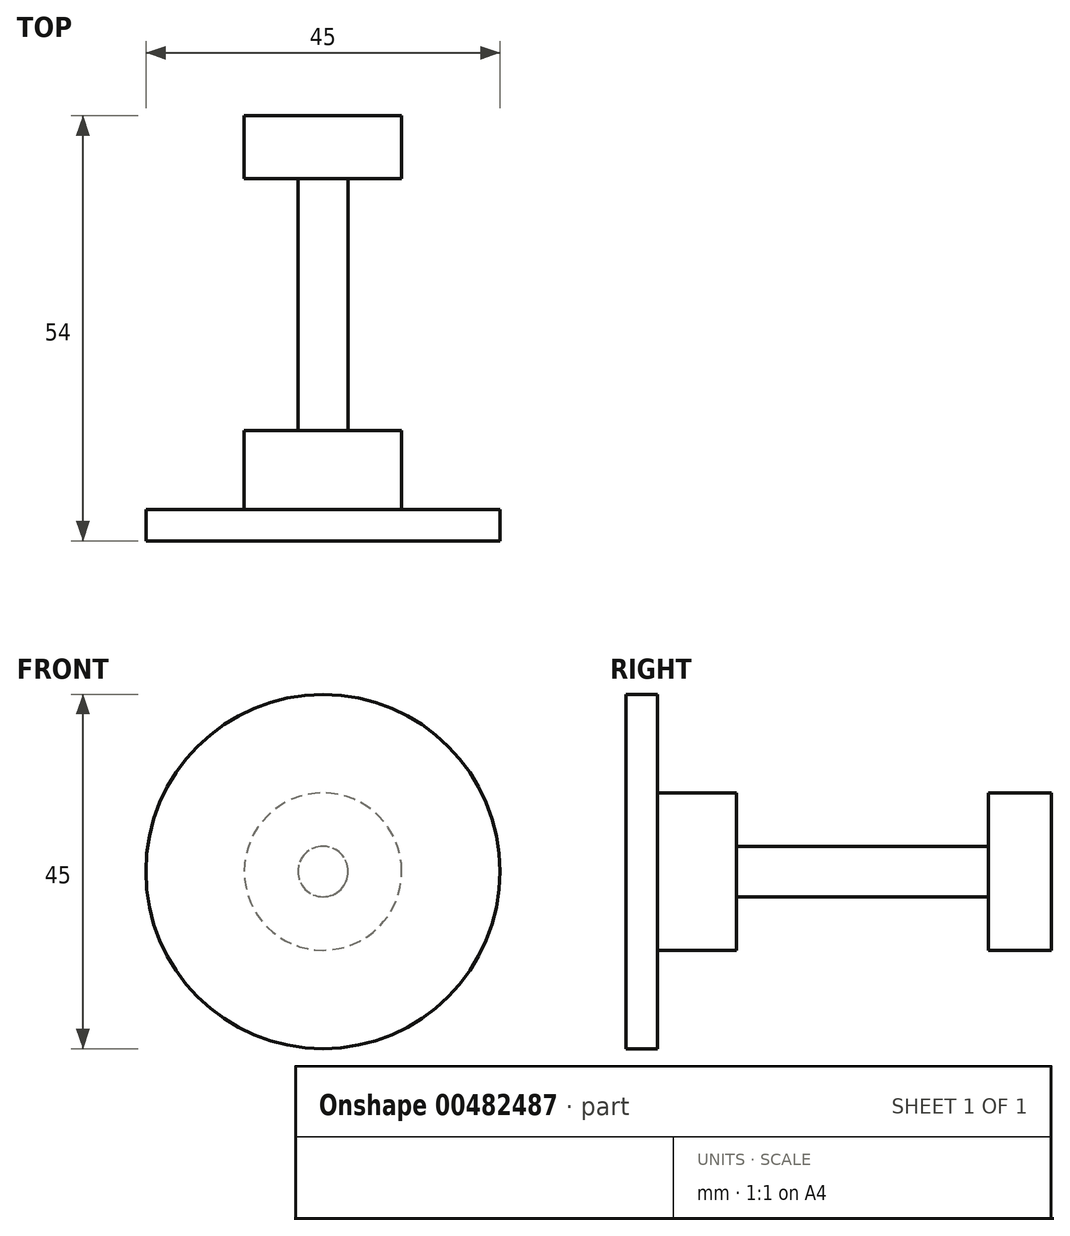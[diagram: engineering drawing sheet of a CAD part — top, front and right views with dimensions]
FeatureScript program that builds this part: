
annotation { "Feature Type Name" : "Feature", "Feature Type Description" : "" }
export const myFeature = defineFeature(function(context is Context, id is Id, definition is map)
    precondition{}
    {
        {
            var Q0;
            Q0=qCreatedBy(makeId("Front.planeOp"),FACE);
            var sketch = newSketch(context, id + "F0", { "sketchPlane" : qUnion([Q0])});
            skCircle(sketch, "E0", {"center": v(-28.73, 70.56) * mm, "radius": 3.2 * mm});
            skSolve(sketch);
        }
        {
            var Q0;
            Q0 = qSketchRegion(id + "F0", true);
            extrude(context, id + "F1", {"entities" : qUnion([Q0]), "depth" : 40 * mm, "offsetDistance" : 25 * mm, "symmetric" : true});
        }
        {
            var Q0;
            Q0=makeQuery(id+"F1.opExtrude","CAP_FACE",FACE,{"disambiguationData":[OSD([sQuery(id+"F0.wireOp",EDGE,"E0")])],"isStart":false});
            var sketch = newSketch(context, id + "F2", { "sketchPlane" : qUnion([Q0])});
            skCircle(sketch, "E1", {"center": v(-28.73, 70.56) * mm, "radius": 10 * mm});
            skSolve(sketch);
        }
        {
            var Q0;
            Q0 = qSketchRegion(id + "F2", true);
            extrude(context, id + "F3", {"entities" : qUnion([Q0]), "operationType" : NewBodyOperationType.ADD, "depth" : 10 * mm, "offsetDistance" : 25 * mm});
        }
        {
            var Q0;
            Q0=makeQuery(id+"F3.opExtrude","CAP_FACE",FACE,{"disambiguationData":[OSD([sQuery(id+"F2.wireOp",EDGE,"E1")])],"isStart":false});
            var sketch = newSketch(context, id + "F4", { "sketchPlane" : qUnion([Q0])});
            skCircle(sketch, "E2", {"center": v(-28.73, 70.56) * mm, "radius": 22.5 * mm});
            skSolve(sketch);
        }
        {
            var Q0;
            Q0=makeQuery(id+"F4.imprint","IMPRINT",FACE,{"disambiguationData":[TD([[makeQuery(id+"F4.imprint","IMPRINT",EDGE,{"derivedFrom":makeQuery(id+"F3.opExtrude","CAP_EDGE",EDGE,{"disambiguationData":[OSD([sQuery(id+"F2.wireOp",EDGE,"E1")])],"isStart":false})}),1.0]])]});
            var Q1;
            Q1=makeQuery(id+"F4.imprint","IMPRINT",FACE,{"disambiguationData":[TD([[makeQuery(id+"F4.imprint","IMPRINT",EDGE,{"derivedFrom":sQuery(id+"F4.wireOp",EDGE,"E2")}),1.0]])]});
            extrude(context, id + "F5", {"entities" : qUnion([Q0, Q1]), "operationType" : NewBodyOperationType.ADD, "depth" : 4 * mm, "offsetDistance" : 25 * mm});
        }
        {
            var Q0;
            Q0=makeQuery(id+"F1.opExtrude","CAP_FACE",FACE,{"disambiguationData":[OSD([sQuery(id+"F0.wireOp",EDGE,"E0")])],"isStart":true});
            var sketch = newSketch(context, id + "F6", { "sketchPlane" : qUnion([Q0])});
            skCircle(sketch, "E3", {"center": v(28.73, 70.56) * mm, "radius": 10 * mm});
            skSolve(sketch);
        }
        {
            var Q0;
            Q0=makeQuery(id+"F6.imprint","IMPRINT",FACE,{"disambiguationData":[TD([[makeQuery(id+"F6.imprint","IMPRINT",EDGE,{"derivedFrom":sQuery(id+"F6.wireOp",EDGE,"E3")}),1.0]])]});
            extrude(context, id + "F7", {"entities" : qUnion([Q0]), "operationType" : NewBodyOperationType.ADD, "oppositeDirection" : true, "depth" : 8 * mm, "offsetDistance" : 25 * mm});
        }
    });
